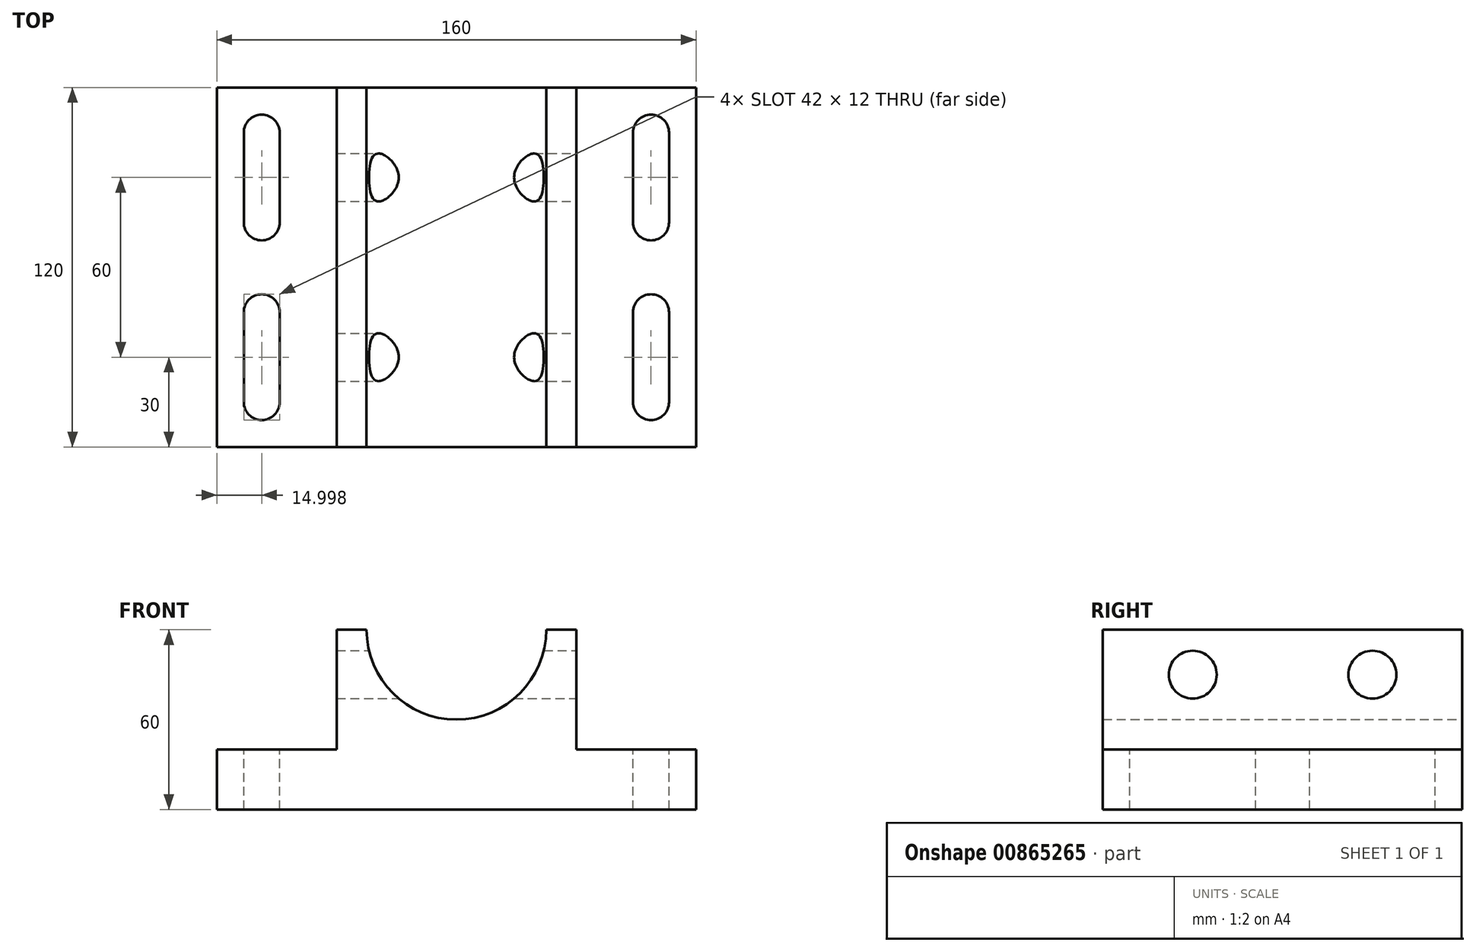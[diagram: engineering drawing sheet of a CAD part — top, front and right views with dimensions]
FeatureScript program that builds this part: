
annotation { "Feature Type Name" : "Feature", "Feature Type Description" : "" }
export const myFeature = defineFeature(function(context is Context, id is Id, definition is map)
    precondition{}
    {
        {
            var Q0;
            Q0=qCreatedBy(makeId("Front.planeOp"),FACE);
            var sketch = newSketch(context, id + "F0", { "sketchPlane" : qUnion([Q0])});
            skLineSegment(sketch, "E0.bottom", {"start": v(-81.44, 48.11) * mm, "end": v(-71.44, 48.11) * mm});
            skLineSegment(sketch, "E0.top", {"start": v(-121.44, -11.89) * mm, "end": v(38.56, -11.89) * mm});
            skLineSegment(sketch, "E0.left", {"start": v(-121.44, 8.11) * mm, "end": v(-121.44, -11.89) * mm});
            skLineSegment(sketch, "E0.right", {"start": v(38.56, 8.11) * mm, "end": v(38.56, -11.89) * mm});
            skLineSegment(sketch, "E1", {"start": v(-81.44, 48.11) * mm, "end": v(-81.44, 8.11) * mm});
            skLineSegment(sketch, "E2", {"start": v(-1.44, 8.11) * mm, "end": v(-1.44, 48.11) * mm});
            skLineSegment(sketch, "E3", {"start": v(-81.44, 8.11) * mm, "end": v(-121.44, 8.11) * mm});
            skLineSegment(sketch, "E4", {"start": v(-1.44, 8.11) * mm, "end": v(38.56, 8.11) * mm});
            skLineSegment(sketch, "E5", {"start": v(-1.44, 48.11) * mm, "end": v(-11.44, 48.11) * mm});
            skArc(sketch, "E6", {"start": v(-71.44, 48.11) * mm, "mid": v(-41.44, 18.11) * mm, "end": v(-11.44, 48.11) * mm});
            skLineSegment(sketch, "E7.trimOffspring", {"start": v(-11.44, 48.11) * mm, "end": v(-1.44, 48.11) * mm});
            skSolve(sketch);
        }
        {
            var Q0;
            Q0 = qSketchRegion(id + "F0", true);
            extrude(context, id + "F1", {"entities" : qUnion([Q0]), "depth" : 60 * mm, "offsetDistance" : 25 * mm});
        }
        {
            var Q0;
            Q0=makeQuery(id+"F1.opExtrude","SWEPT_FACE",FACE,{"disambiguationData":[OSD([sQuery(id+"F0.wireOp",EDGE,"E4")])]});
            var sketch = newSketch(context, id + "F2", { "sketchPlane" : qUnion([Q0])});
            skLineSegment(sketch, "E8", {"start": v(38.56, 0) * mm, "end": v(38.56, -30) * mm});
            skArc(sketch, "E9", {"start": v(29.56, -15) * mm, "mid": v(23.56, -9) * mm, "end": v(17.56, -15) * mm});
            skArc(sketch, "E10", {"start": v(17.56, -45) * mm, "mid": v(23.56, -51) * mm, "end": v(29.56, -45) * mm});
            skLineSegment(sketch, "E11", {"start": v(29.56, -15) * mm, "end": v(29.56, -45) * mm});
            skLineSegment(sketch, "E12", {"start": v(17.56, -15) * mm, "end": v(17.56, -45) * mm});
            skSolve(sketch);
        }
        {
            var Q0;
            Q0 = qSketchRegion(id + "F2", true);
            extrude(context, id + "F3", {"entities" : qUnion([Q0]), "operationType" : NewBodyOperationType.REMOVE, "oppositeDirection" : true, "depth" : 20 * mm, "offsetDistance" : 25 * mm});
        }
        {
            var Q0;
            Q0=makeQuery(id+"F1.opExtrude","SWEPT_FACE",FACE,{"disambiguationData":[OSD([sQuery(id+"F0.wireOp",EDGE,"E3")])]});
            var sketch = newSketch(context, id + "F4", { "sketchPlane" : qUnion([Q0])});
            skPoint(sketch, "E13.orphan", {"position": v(-106.44, -60) * mm});
            skArc(sketch, "E14", {"start": v(-112.44, -45) * mm, "mid": v(-106.44, -51) * mm, "end": v(-100.44, -45) * mm});
            skArc(sketch, "E15", {"start": v(-100.44, -15) * mm, "mid": v(-106.44, -9) * mm, "end": v(-112.44, -15) * mm});
            skLineSegment(sketch, "E16", {"start": v(-100.44, -15) * mm, "end": v(-100.44, -45) * mm});
            skLineSegment(sketch, "E17", {"start": v(-112.44, -15) * mm, "end": v(-112.44, -45) * mm});
            skSolve(sketch);
        }
        {
            var Q0;
            Q0 = qSketchRegion(id + "F4", true);
            extrude(context, id + "F5", {"entities" : qUnion([Q0]), "operationType" : NewBodyOperationType.REMOVE, "oppositeDirection" : true, "depth" : 20 * mm, "offsetDistance" : 25 * mm});
        }
        {
            var Q0;
            Q0=makeQuery(id+"F1.opExtrude","SWEPT_FACE",FACE,{"disambiguationData":[OSD([sQuery(id+"F0.wireOp",EDGE,"E2")])]});
            var sketch = newSketch(context, id + "F6", { "sketchPlane" : qUnion([Q0])});
            skCircle(sketch, "E18", {"center": v(-30, 33.11) * mm, "radius": 8 * mm});
            skPoint(sketch, "E19.end.orphan", {"position": v(-30, 48.11) * mm});
            skSolve(sketch);
        }
        {
            var Q0;
            Q0 = qSketchRegion(id + "F6", true);
            extrude(context, id + "F7", {"entities" : qUnion([Q0]), "operationType" : NewBodyOperationType.REMOVE, "oppositeDirection" : true, "depth" : 80 * mm, "offsetDistance" : 25 * mm});
        }
        {
            var Q0;
            Q0=makeQuery(id+"F1.opExtrude","SWEPT_BODY",BODY,{"disambiguationData":[OSD([sQuery(id+"F0.wireOp",EDGE,"E0.bottom"),sQuery(id+"F0.wireOp",EDGE,"E0.top"),sQuery(id+"F0.wireOp",EDGE,"E0.left"),sQuery(id+"F0.wireOp",EDGE,"E0.right"),sQuery(id+"F0.wireOp",EDGE,"E1"),sQuery(id+"F0.wireOp",EDGE,"E2"),sQuery(id+"F0.wireOp",EDGE,"E3"),sQuery(id+"F0.wireOp",EDGE,"E4"),sQuery(id+"F0.wireOp",EDGE,"E6"),sQuery(id+"F0.wireOp",EDGE,"E7.trimOffspring")])]});
            var Q1;
            Q1=makeQuery(id+"F1.opExtrude","CAP_FACE",FACE,{"disambiguationData":[OSD([sQuery(id+"F0.wireOp",EDGE,"E0.bottom"),sQuery(id+"F0.wireOp",EDGE,"E0.top"),sQuery(id+"F0.wireOp",EDGE,"E0.left"),sQuery(id+"F0.wireOp",EDGE,"E0.right"),sQuery(id+"F0.wireOp",EDGE,"E1"),sQuery(id+"F0.wireOp",EDGE,"E2"),sQuery(id+"F0.wireOp",EDGE,"E3"),sQuery(id+"F0.wireOp",EDGE,"E4"),sQuery(id+"F0.wireOp",EDGE,"E6"),sQuery(id+"F0.wireOp",EDGE,"E7.trimOffspring")])],"isStart":false});
            mirror(context, id + "F8", {"operationType" : NewBodyOperationType.ADD, "entities" : qUnion([Q0]), "mirrorPlane" : qUnion([Q1])});
        }
    });
